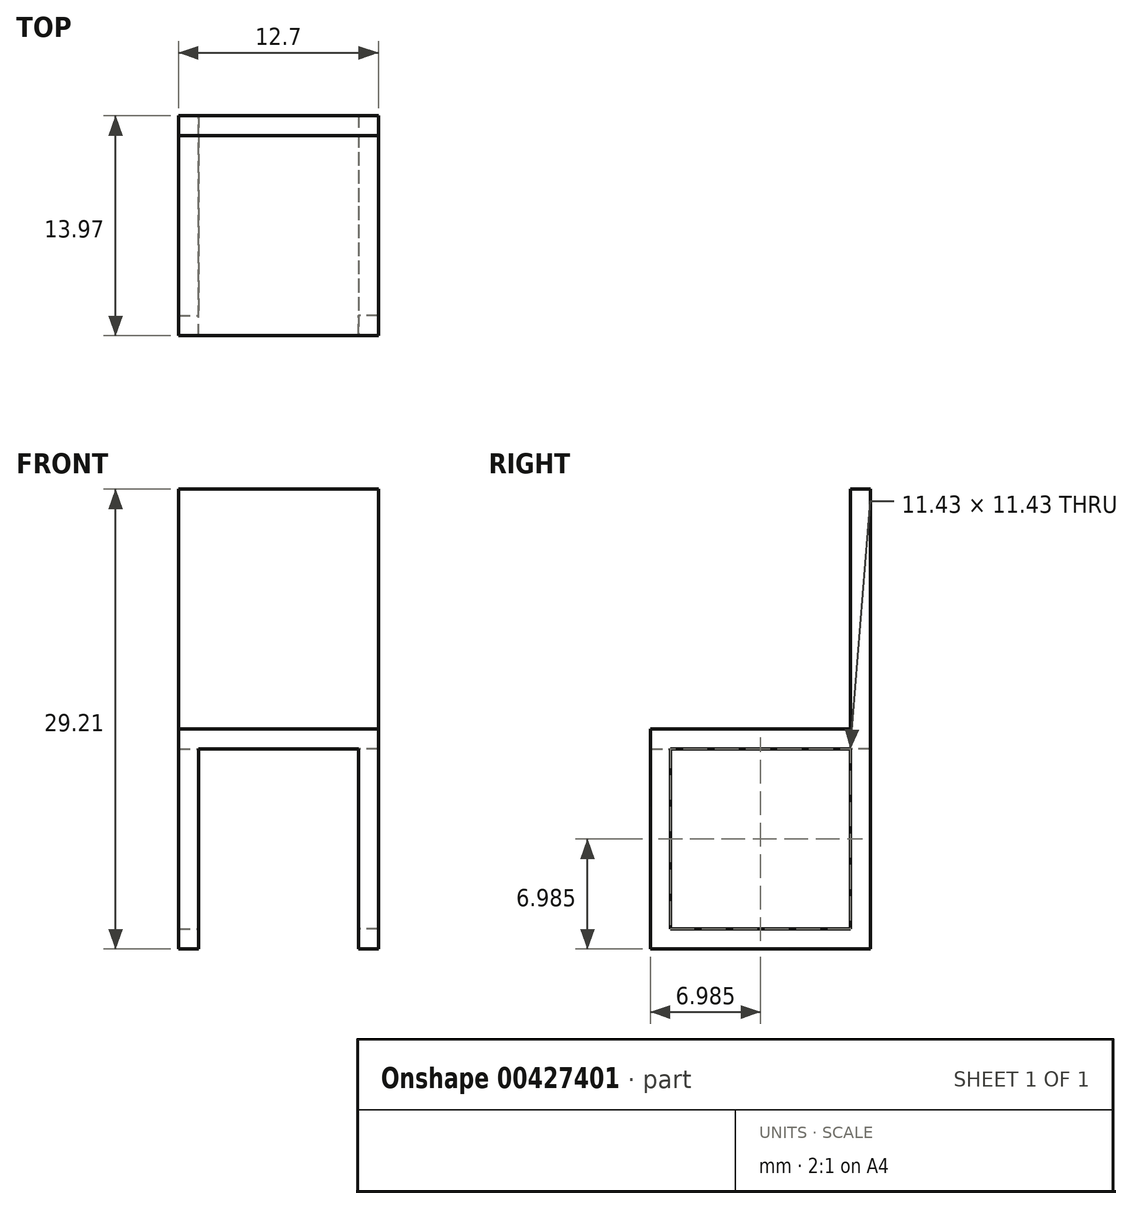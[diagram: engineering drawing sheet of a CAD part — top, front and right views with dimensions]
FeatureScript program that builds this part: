
annotation { "Feature Type Name" : "Feature", "Feature Type Description" : "" }
export const myFeature = defineFeature(function(context is Context, id is Id, definition is map)
    precondition{}
    {
        {
            var Q0;
            Q0=qCreatedBy(makeId("Front.planeOp"),FACE);
            var sketch = newSketch(context, id + "F0", { "sketchPlane" : qUnion([Q0])});
            skLineSegment(sketch, "E0", {"start": v(0, 0) * mm, "end": v(-6.35, 0) * mm});
            skLineSegment(sketch, "E1", {"start": v(-6.35, 0) * mm, "end": v(-6.35, 1.27) * mm});
            skLineSegment(sketch, "E2", {"start": v(-6.35, 1.27) * mm, "end": v(0, 1.27) * mm});
            skLineSegment(sketch, "E3.MirrorCS", {"start": v(0, 0) * mm, "end": v(6.35, 0) * mm});
            skLineSegment(sketch, "E4.MirrorCS", {"start": v(6.35, 1.27) * mm, "end": v(0, 1.27) * mm});
            skLineSegment(sketch, "E5.MirrorCS", {"start": v(6.35, 0) * mm, "end": v(6.35, 1.27) * mm});
            skSolve(sketch);
        }
        {
            var Q0;
            Q0=qSketchRegion(id+"F0",true);
            extrude(context, id + "F1", {"entities" : qUnion([Q0]), "depth" : 13.97 * mm});
        }
        {
            var Q0;
            Q0=makeQuery(id+"F1.opExtrude","SWEPT_FACE",FACE,{"disambiguationData":[OSD([sQuery(id+"F0.wireOp",EDGE,"E2"),sQuery(id+"F0.wireOp",EDGE,"E4.MirrorCS")])]});
            var sketch = newSketch(context, id + "F2", { "sketchPlane" : qUnion([Q0])});
            skLineSegment(sketch, "E6", {"start": v(6.35, 0) * mm, "end": v(6.35, -1.26) * mm});
            skLineSegment(sketch, "E7", {"start": v(6.35, -1.26) * mm, "end": v(-6.35, -1.26) * mm});
            skLineSegment(sketch, "E8", {"start": v(-6.35, -1.26) * mm, "end": v(-6.35, 0) * mm});
            skLineSegment(sketch, "E9", {"start": v(-6.35, 0) * mm, "end": v(6.35, 0) * mm});
            skSolve(sketch);
        }
        {
            var Q0;
            Q0=qSketchRegion(id+"F2",true);
            extrude(context, id + "F3", {"entities" : qUnion([Q0]), "operationType" : NewBodyOperationType.ADD, "depth" : 15.24 * mm});
        }
        {
            var Q0;
            Q0=makeQuery(id+"F1.opExtrude","SWEPT_FACE",FACE,{"disambiguationData":[OSD([sQuery(id+"F0.wireOp",EDGE,"E0"),sQuery(id+"F0.wireOp",EDGE,"E3.MirrorCS")])]});
            var sketch = newSketch(context, id + "F4", { "sketchPlane" : qUnion([Q0])});
            skLineSegment(sketch, "E10.bottom", {"start": v(-6.35, 13.97) * mm, "end": v(-5.08, 13.97) * mm});
            skLineSegment(sketch, "E10.top", {"start": v(-6.35, 12.7) * mm, "end": v(-5.08, 12.7) * mm});
            skLineSegment(sketch, "E10.left", {"start": v(-6.35, 13.97) * mm, "end": v(-6.35, 12.7) * mm});
            skLineSegment(sketch, "E10.right", {"start": v(-5.08, 13.97) * mm, "end": v(-5.08, 12.7) * mm});
            skLineSegment(sketch, "E11.bottom", {"start": v(-6.35, 0) * mm, "end": v(-5.08, 0) * mm});
            skLineSegment(sketch, "E11.top", {"start": v(-6.35, 1.27) * mm, "end": v(-5.08, 1.27) * mm});
            skLineSegment(sketch, "E11.left", {"start": v(-6.35, 0) * mm, "end": v(-6.35, 1.27) * mm});
            skLineSegment(sketch, "E11.right", {"start": v(-5.08, 0) * mm, "end": v(-5.08, 1.27) * mm});
            skLineSegment(sketch, "E12.MirrorCS", {"start": v(6.35, 1.27) * mm, "end": v(5.08, 1.27) * mm});
            skLineSegment(sketch, "E13.MirrorCS", {"start": v(6.35, 0) * mm, "end": v(6.35, 1.27) * mm});
            skLineSegment(sketch, "E14.MirrorCS", {"start": v(5.08, 0) * mm, "end": v(5.08, 1.27) * mm});
            skLineSegment(sketch, "E15.MirrorCS", {"start": v(6.35, 0) * mm, "end": v(5.08, 0) * mm});
            skLineSegment(sketch, "E16.MirrorCS", {"start": v(6.35, 13.97) * mm, "end": v(5.08, 13.97) * mm});
            skLineSegment(sketch, "E17.MirrorCS", {"start": v(5.08, 13.97) * mm, "end": v(5.08, 12.7) * mm});
            skLineSegment(sketch, "E18.MirrorCS", {"start": v(6.35, 12.7) * mm, "end": v(5.08, 12.7) * mm});
            skLineSegment(sketch, "E19.MirrorCS", {"start": v(6.35, 13.97) * mm, "end": v(6.35, 12.7) * mm});
            skSolve(sketch);
        }
        {
            var Q0;
            Q0=qSketchRegion(id+"F4",true);
            extrude(context, id + "F5", {"entities" : qUnion([Q0]), "operationType" : NewBodyOperationType.ADD, "depth" : 12.7 * mm});
        }
        {
            var Q0;
            Q0=makeQuery(id+"F5.opExtrude","SWEPT_FACE",FACE,{"disambiguationData":[OSD([sQuery(id+"F4.wireOp",EDGE,"E18.MirrorCS")])]});
            var sketch = newSketch(context, id + "F6", { "sketchPlane" : qUnion([Q0])});
            skLineSegment(sketch, "E20.bottom", {"start": v(-5.08, -12.7) * mm, "end": v(-6.35, -12.7) * mm});
            skLineSegment(sketch, "E20.top", {"start": v(-5.08, -11.43) * mm, "end": v(-6.35, -11.43) * mm});
            skLineSegment(sketch, "E20.left", {"start": v(-5.08, -12.7) * mm, "end": v(-5.08, -11.43) * mm});
            skLineSegment(sketch, "E20.right", {"start": v(-6.35, -12.7) * mm, "end": v(-6.35, -11.43) * mm});
            skSolve(sketch);
        }
        {
            var Q0;
            Q0=qSketchRegion(id+"F6",true);
            extrude(context, id + "F7", {"entities" : qUnion([Q0]), "operationType" : NewBodyOperationType.ADD, "depth" : 12.7 * mm});
        }
        {
            var Q0;
            Q0=makeQuery(id+"F1.opExtrude","SWEPT_BODY",BODY,{"disambiguationData":[OSD([sQuery(id+"F0.wireOp",EDGE,"E0"),sQuery(id+"F0.wireOp",EDGE,"E1"),sQuery(id+"F0.wireOp",EDGE,"E2"),sQuery(id+"F0.wireOp",EDGE,"E3.MirrorCS"),sQuery(id+"F0.wireOp",EDGE,"E4.MirrorCS"),sQuery(id+"F0.wireOp",EDGE,"E5.MirrorCS")])]});
            var Q1;
            Q1=qCreatedBy(makeId("Right.planeOp"),FACE);
            mirror(context, id + "F8", {"operationType" : NewBodyOperationType.ADD, "entities" : qUnion([Q0]), "mirrorPlane" : qUnion([Q1])});
        }
    });
